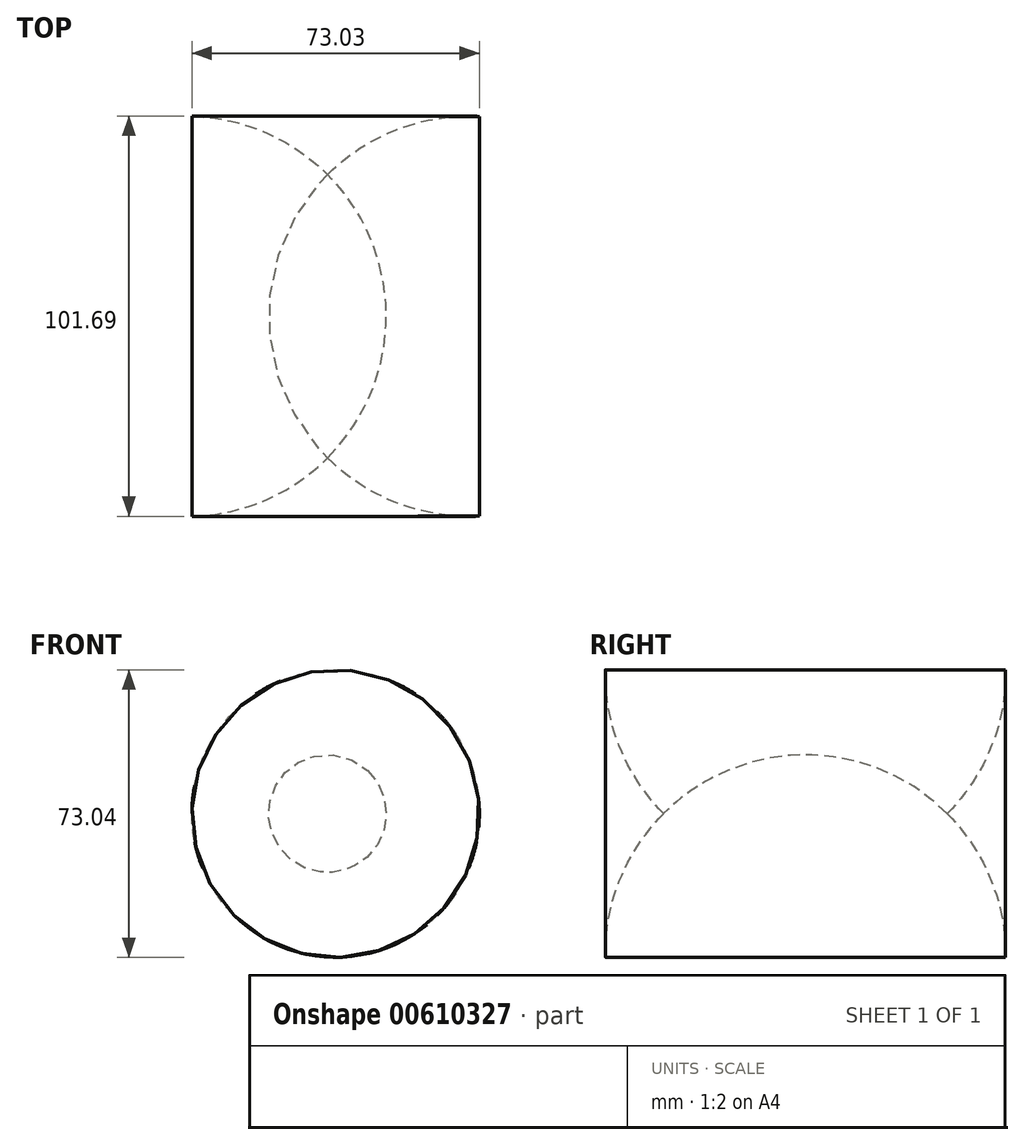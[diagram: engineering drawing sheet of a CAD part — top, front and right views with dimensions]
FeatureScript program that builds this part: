
annotation { "Feature Type Name" : "Feature", "Feature Type Description" : "" }
export const myFeature = defineFeature(function(context is Context, id is Id, definition is map)
    precondition{}
    {
        {
            var Q0;
            Q0=qCreatedBy(makeId("Top.planeOp"),FACE);
            var sketch = newSketch(context, id + "F0", { "sketchPlane" : qUnion([Q0])});
            skFitSpline(sketch, "E0", {"points": [v(-30.16, 26.85) * mm, v(-42.83, 13.08) * mm, v(-32.36, -8.95) * mm, v(-34.29, -27.68) * mm, v(7.02, -6.75) * mm, v(28.23, -18.6) * mm, v(31.81, -15.01) * mm, v(27.68, 21.9) * mm, v(12.53, 28.78) * mm, v(-11.98, 56.32) * mm, v(-23, 38.7) * mm, v(-20.8, 35.12) * mm, v(-19.42, 8.4) * mm, v(-30.16, 26.85) * mm]});
            skSolve(sketch);
        }
        {
            var Q0;
            Q0=makeQuery(id+"F0.imprint","IMPRINT",FACE,{"disambiguationData":[TD([[makeQuery(id+"F0.imprint","IMPRINT",EDGE,{"derivedFrom":sQuery(id+"F0.wireOp",EDGE,"E0")}),1.0]])]});
            extrude(context, id + "F1", {"entities" : qUnion([Q0]), "depth" : 152.4 * mm, "offsetDistance" : 25.4 * mm});
        }
        {
            var Q0;
            Q0=makeQuery(id+"F1.opExtrude","SWEPT_BODY",BODY,{"disambiguationData":[OSD([sQuery(id+"F0.wireOp",EDGE,"E0")])]});
            deleteBodies(context, id + "F2", {"entities" : qUnion([Q0])});
        }
        {
            var Q0;
            Q0=qCreatedBy(makeId("Top.planeOp"),FACE);
            var sketch = newSketch(context, id + "F3", { "sketchPlane" : qUnion([Q0])});
            skLineSegment(sketch, "E1", {"start": v(-16.25, 66.04) * mm, "end": v(-16.25, -69.33) * mm, "construction": true});
            skArc(sketch, "E2", {"start": v(-16.25, 29) * mm, "mid": v(-102.99, -7) * mm, "end": v(-16.25, -43) * mm});
            skLineSegment(sketch, "E3", {"start": v(-16.25, 29) * mm, "end": v(-16.25, -43) * mm});
            skSolve(sketch);
        }
        {
            var Q0;
            Q0=makeQuery(id+"F3.imprint","IMPRINT",FACE,{"disambiguationData":[TD([[makeQuery(id+"F3.imprint","IMPRINT",EDGE,{"derivedFrom":sQuery(id+"F3.wireOp",EDGE,"E2")}),1.0]])]});
            var Q1;
            Q1=sQuery(id+"F3.wireOp",EDGE,"E1");
            revolve(context, id + "F4", {"surfaceOperationType" : NewSurfaceOperationType.NEW, "entities" : qUnion([Q0]), "axis" : qUnion([Q1]), "revolveType" : RevolveType.FULL});
        }
        {
            var Q0;
            Q0=qCreatedBy(makeId("Front.planeOp"),FACE);
            var sketch = newSketch(context, id + "F5", { "sketchPlane" : qUnion([Q0])});
            skCircle(sketch, "E4", {"center": v(-14.2, 0) * mm, "radius": 36.52 * mm});
            skSolve(sketch);
        }
        {
            var Q0;
            Q0 = qSketchRegion(id + "F5", true);
            extrude(context, id + "F6", {"entities" : qUnion([Q0]), "operationType" : NewBodyOperationType.REMOVE, "endBound" : BoundingType.SYMMETRIC, "oppositeDirection" : true, "depth" : 152.4 * mm, "offsetDistance" : 25.4 * mm});
        }
    });
